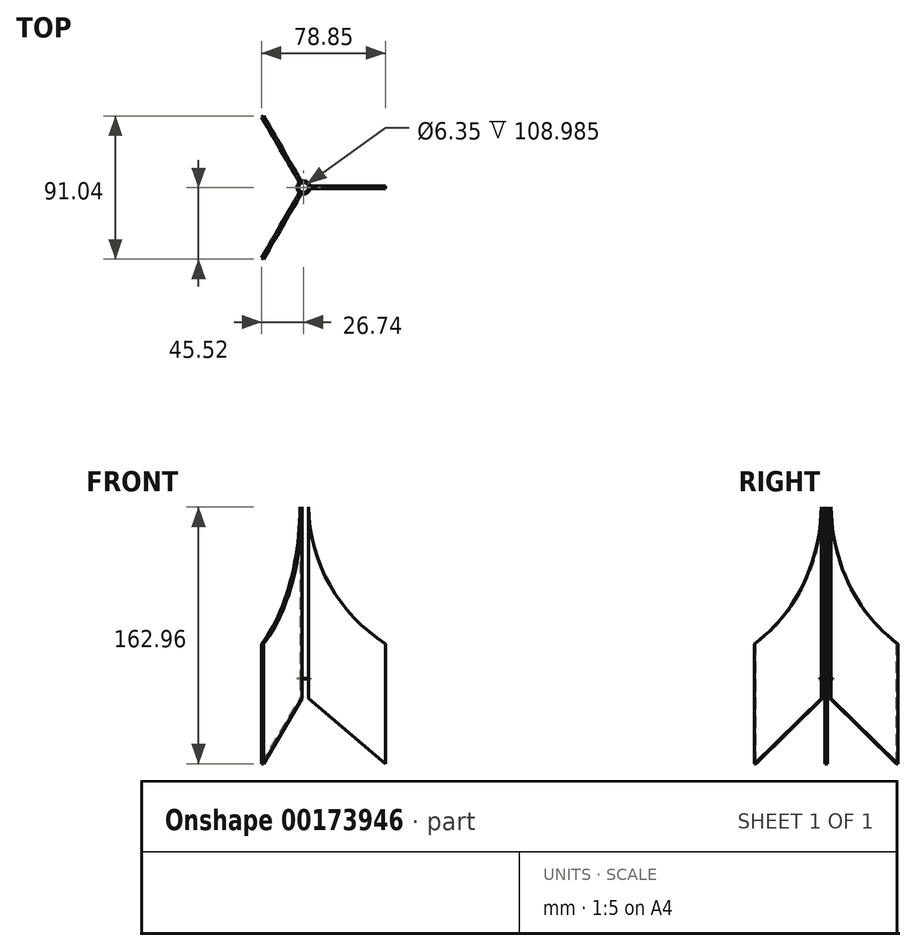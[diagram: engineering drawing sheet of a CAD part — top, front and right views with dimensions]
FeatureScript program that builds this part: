
annotation { "Feature Type Name" : "Feature", "Feature Type Description" : "" }
export const myFeature = defineFeature(function(context is Context, id is Id, definition is map)
    precondition{}
    {
        {
            var Q0;
            Q0=qCreatedBy(makeId("Top.planeOp"),FACE);
            var sketch = newSketch(context, id + "F0", { "sketchPlane" : qUnion([Q0])});
            skCircle(sketch, "E0", {"center": v(0, 0) * mm, "radius": 4.2 * mm});
            skCircle(sketch, "E1", {"center": v(0, 0) * mm, "radius": 2.92 * mm});
            skSolve(sketch);
        }
        {
            var Q0;
            Q0=makeQuery(id+"F0.imprint","IMPRINT",FACE,{"disambiguationData":[TD([[makeQuery(id+"F0.imprint","IMPRINT",EDGE,{"derivedFrom":sQuery(id+"F0.wireOp",EDGE,"E0")}),1.0]])]});
            extrude(context, id + "F1", {"entities" : qUnion([Q0]), "depth" : 35 / 203.2 * mm, "offsetDistance" : 25.4 * mm});
        }
        {
            var Q0;
            Q0=qCreatedBy(makeId("Front.planeOp"),FACE);
            var sketch = newSketch(context, id + "F2", { "sketchPlane" : qUnion([Q0])});
            skLineSegment(sketch, "E2", {"start": v(3.05, 111.12) * mm, "end": v(3.05, -12.62) * mm});
            skLineSegment(sketch, "E3", {"start": v(3.05, -12.62) * mm, "end": v(52.1, -12.62) * mm});
            skLineSegment(sketch, "E4", {"start": v(52.1, -12.62) * mm, "end": v(52.1, 22.2) * mm});
            skLineSegment(sketch, "E5", {"start": v(52.1, 22.2) * mm, "end": v(52.1, -12.62) * mm});
            skLineSegment(sketch, "E6", {"start": v(52.1, -12.62) * mm, "end": v(52.1, -53.97) * mm});
            skPoint(sketch, "E6.endSnap0", {"position": v(52.1, 4.79) * mm});
            skLineSegment(sketch, "E7", {"start": v(52.1, -53.97) * mm, "end": v(3.05, -12.62) * mm});
            skArc(sketch, "E8", {"start": v(3.05, 111.12) * mm, "mid": v(16.13, 60.34) * mm, "end": v(52.1, 22.2) * mm});
            skLineSegment(sketch, "E9", {"start": v(0, 167.4) * mm, "end": v(0, -117.6) * mm, "construction": true});
            skSolve(sketch);
        }
        {
            var Q0;
            Q0=makeQuery(id+"F2.imprint","IMPRINT",FACE,{"disambiguationData":[TD([[makeQuery(id+"F2.imprint","IMPRINT",EDGE,{"derivedFrom":sQuery(id+"F2.wireOp",EDGE,"E2")}),1.0]])]});
            var Q1;
            Q1=makeQuery(id+"F2.imprint","IMPRINT",FACE,{"disambiguationData":[TD([[makeQuery(id+"F2.imprint","IMPRINT",EDGE,{"derivedFrom":sQuery(id+"F2.wireOp",EDGE,"E3")}),-1.0]])]});
            extrude(context, id + "F3", {"entities" : qUnion([Q0, Q1]), "depth" : 0.8 * mm, "offsetDistance" : 25.4 * mm, "hasSecondDirection" : true, "secondDirectionOppositeDirection" : true, "secondDirectionDepth" : 0.8 * mm});
        }
        {
            var Q0;
            Q0=makeQuery(id+"F3.opExtrude","SWEPT_BODY",BODY,{"disambiguationData":[OSD([sQuery(id+"F2.wireOp",EDGE,"E2"),sQuery(id+"F2.wireOp",EDGE,"E5"),sQuery(id+"F2.wireOp",EDGE,"E6"),sQuery(id+"F2.wireOp",EDGE,"E7"),sQuery(id+"F2.wireOp",EDGE,"E8")])]});
            var Q1;
            Q1=sQuery(id+"F2.wireOp",EDGE,"E9");
            circularPattern(context, id + "F4", {"operationType" : NewBodyOperationType.ADD, "entities" : qUnion([Q0]), "axis" : qUnion([Q1]), "angle" : 360 * degree, "instanceCount" : 3, "equalSpace" : true});
        }
        {
            var Q0;
            Q0=sQuery(id+"F0.wireOp",VERTEX,"E0.center");
            var Q1;
            Q1=makeQuery(id+"F1.opExtrude","SWEPT_BODY",BODY,{"disambiguationData":[OSD([sQuery(id+"F0.wireOp",EDGE,"E0")])]});
            hole(context, id + "F5", {"style" : HoleStyle.SIMPLE, "endStyle" : HoleEndStyle.THROUGH, "oppositeDirection" : true, "holeDiameter" : 6.35 * mm, "locations" : qUnion([Q0]), "scope" : qUnion([Q1]), "isTappedThrough" : true});
        }
    });
